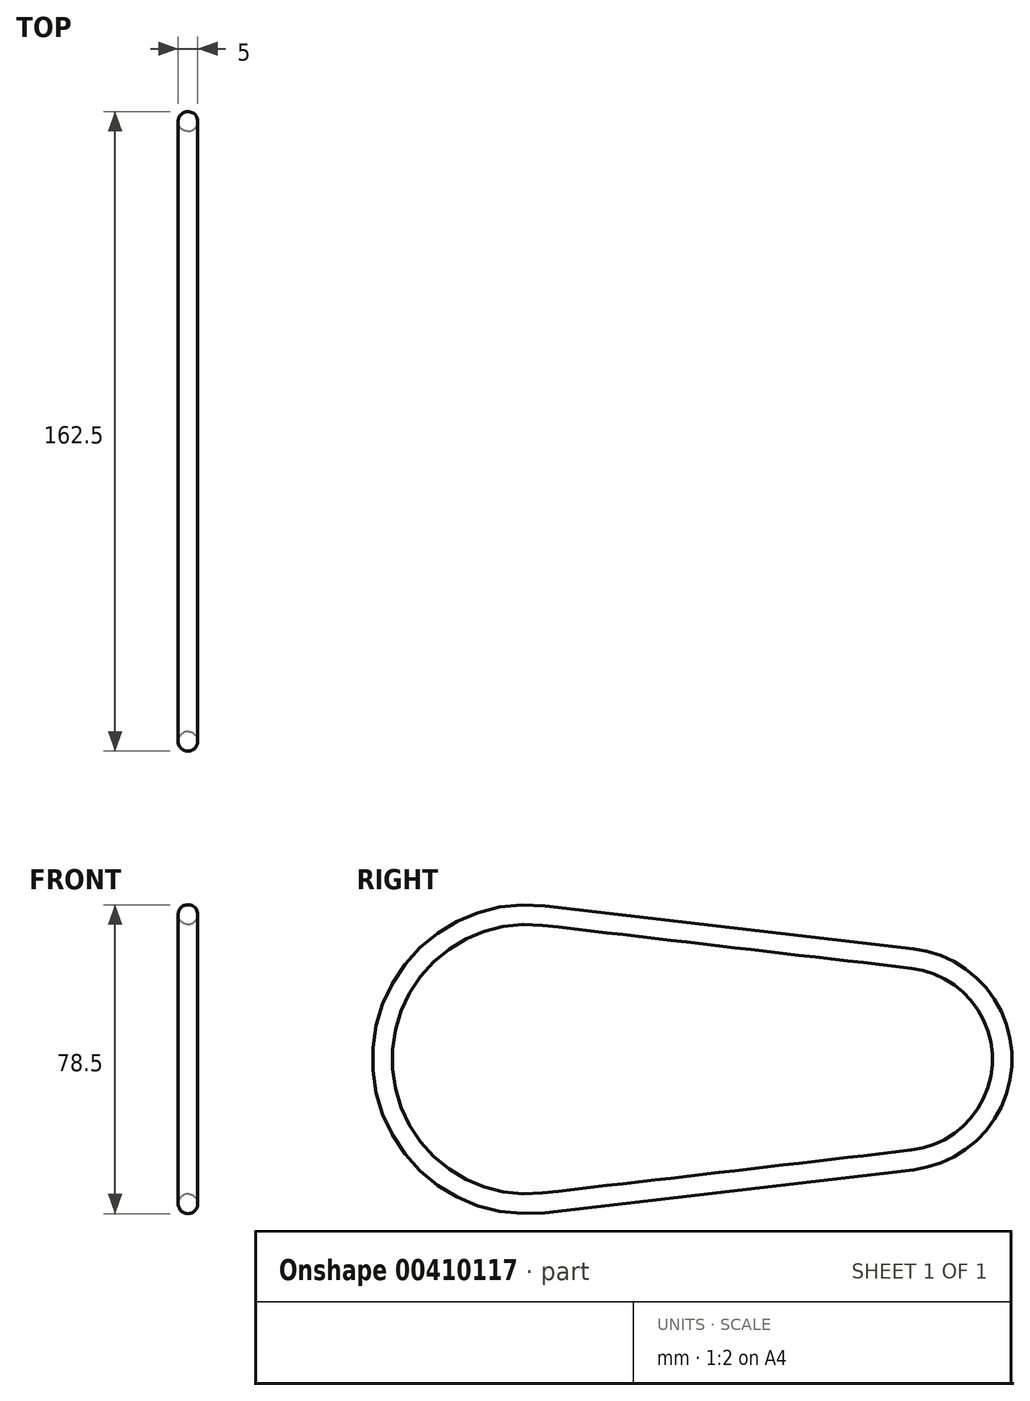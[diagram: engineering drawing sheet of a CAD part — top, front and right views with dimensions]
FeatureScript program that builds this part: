
annotation { "Feature Type Name" : "Feature", "Feature Type Description" : "" }
export const myFeature = defineFeature(function(context is Context, id is Id, definition is map)
    precondition{}
    {
        {
            var Q0;
            Q0=qCreatedBy(makeId("Right.planeOp"),FACE);
            var sketch = newSketch(context, id + "F0", { "sketchPlane" : qUnion([Q0])});
            skLineSegment(sketch, "E0", {"start": v(0, 0) * mm, "end": v(95, 0) * mm, "construction": true});
            skArc(sketch, "E1", {"start": v(4.28, 36.75) * mm, "mid": v(-37, 0) * mm, "end": v(4.28, -36.75) * mm});
            skArc(sketch, "E2", {"start": v(98.01, -25.83) * mm, "mid": v(121, 0) * mm, "end": v(98.01, 25.83) * mm});
            skLineSegment(sketch, "E3", {"start": v(4.28, 36.75) * mm, "end": v(98.01, 25.83) * mm});
            skLineSegment(sketch, "E4", {"start": v(4.28, -36.75) * mm, "end": v(98.01, -25.83) * mm});
            skSolve(sketch);
        }
        {
            var Q0;
            Q0=qCreatedBy(makeId("Front.planeOp"),FACE);
            var sketch = newSketch(context, id + "F1", { "sketchPlane" : qUnion([Q0])});
            skCircle(sketch, "E5", {"center": v(0, 36.75) * mm, "radius": 2.5 * mm});
            skSolve(sketch);
        }
        {
            var Q0;
            Q0=makeQuery(id+"F1.imprint","IMPRINT",FACE,{"disambiguationData":[TD([[makeQuery(id+"F1.imprint","IMPRINT",EDGE,{"derivedFrom":sQuery(id+"F1.wireOp",EDGE,"E5")}),1.0]])]});
            var Q1;
            Q1=sQuery(id+"F0.wireOp",EDGE,"E1");
            var Q2;
            Q2=sQuery(id+"F0.wireOp",EDGE,"E4");
            var Q3;
            Q3=sQuery(id+"F0.wireOp",EDGE,"E2");
            var Q4;
            Q4=sQuery(id+"F0.wireOp",EDGE,"E3");
            sweep(context, id + "F2", {"profiles" : qUnion([Q0]), "path" : qUnion([Q1, Q2, Q3, Q4])});
        }
    });
